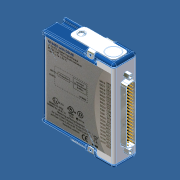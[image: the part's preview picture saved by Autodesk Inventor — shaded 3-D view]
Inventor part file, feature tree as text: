
AUTODESK INVENTOR PART (.ipt)
format: ipt  version: unknown  size: 13,053,440 bytes
history: native  units: mm
features: other x7, sketch x5, pattern_linear x3, revolve x2, imported_body x1, extrude x1
ambient origin geometry x8: Origin, YZ Plane, XZ Plane, XY Plane, X Axis, Y Axis, Z Axis, Center Point
bodies: Solid1 (feature_tree)
feature tree (19):
  imported_body  "Base1"
  other  "RIGHT"
  other  "TOP"
  other  "FRONT"
  extrude  "Extrusion1"  Depth=190.0mm
  pattern_linear  "Rectangular Pattern1"  Count1=19 Spacing1=2.7432mm
  revolve  "Revolution1"  Angle=180.0deg
  pattern_linear  "Rectangular Pattern2"  Count1=18 Spacing1=2.7432mm
  revolve  "Revolution2"  [1 undecoded]
  pattern_linear  "Rectangular Pattern3"  Spacing1=0.0mm  [1 undecoded]
  other  "Decal4"
  other  "Decal5"
  sketch  "Sketch1"  dims[d4=5.461mm d5=0.0mm d6=190.0mm d8=2.7432mm]
  sketch  "Sketch2"  dims[d10=1.016mm]
  sketch  "Sketch3"  dims[d11=1.016mm]
  sketch  "Sketch7"  dims[d12=180.0deg d13=190.0mm d15=2.7432mm]
  other  "Image8"
  sketch  "Sketch8"  dims[d16=180.0deg d17=180.0deg d18=180.0mm d20=2.7432mm d159=25.4mm d160=0.0mm d173=74.93mm d174=0.0mm d175=0.0mm]
  other  "Image10"
note: 2 required parameter values undecoded (feature->parameter linkage not recoverable at this tier; creation-order binding heuristic only, values carry confidence <= 0.55)